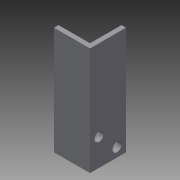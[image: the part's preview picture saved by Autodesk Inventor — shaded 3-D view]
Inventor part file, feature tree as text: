
AUTODESK INVENTOR PART (.ipt)
format: ipt  version: 2015 SP1 (Build 190203100, 203)  size: 88,064 bytes
history: native  units: in
note: dims shown in document units (in); Inventor stores cm internally (conversion verified against a paired STEP export)
features: sketch x2, extrude x1, hole x1
ambient origin geometry x8: Origin, YZ Plane, XZ Plane, XY Plane, X Axis, Y Axis, Z Axis, Center Point
bodies: Solid1 (feature_tree)
feature tree (4):
  extrude  "Extrusion1"  Depth=0.125in
  hole  "Hole1"  [1 undecoded]
  sketch  "Sketch1"  dims[d0=1.0in d1=0.125in]
  sketch  "Sketch2"  dims[d2=0.125in d3=1.0in d4=3.0in d5=0.0in d6=0.25in d7=0.25in d8=0.75in d9=0.75in d10=0.25in d11=0.75in d12=0.375in d13=0.25in d14=0.5635in d15=1.0in d16=0.8108in]
note: 1 required parameter value undecoded (feature->parameter linkage not recoverable at this tier; creation-order binding heuristic only, values carry confidence <= 0.55)
